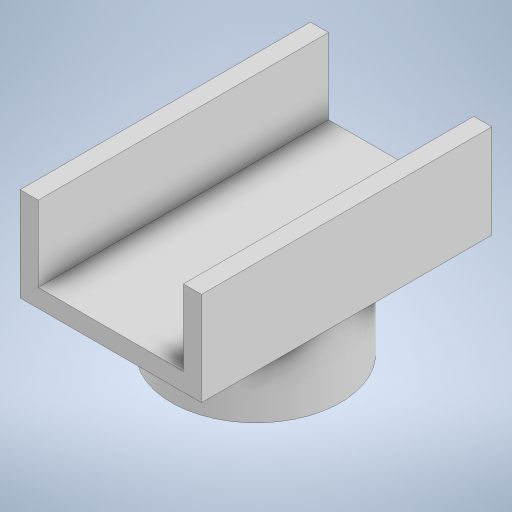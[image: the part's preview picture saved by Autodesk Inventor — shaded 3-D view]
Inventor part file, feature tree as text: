
AUTODESK INVENTOR PART (.ipt)
format: ipt  version: 2024 (Build 280153000, 153)  size: 239,104 bytes
history: native  units: mm
features: extrude x3, other x1, sketch x1, projected_geometry x1
ambient origin geometry x8: Origin, YZ Plane, XZ Plane, XY Plane, X Axis, Y Axis, Z Axis, Center Point
bodies: Body1 (feature_tree)
feature tree (6):
  other  "솔리드1"
  extrude  "돌출1"  Depth=4.8mm
  extrude  "돌출2"  Depth=9.6mm
  extrude  "돌출5"  Depth=0.6mm TaperAngle=0.0deg
  sketch  "스케치2"
  projected_geometry  "투영된 루프1"
